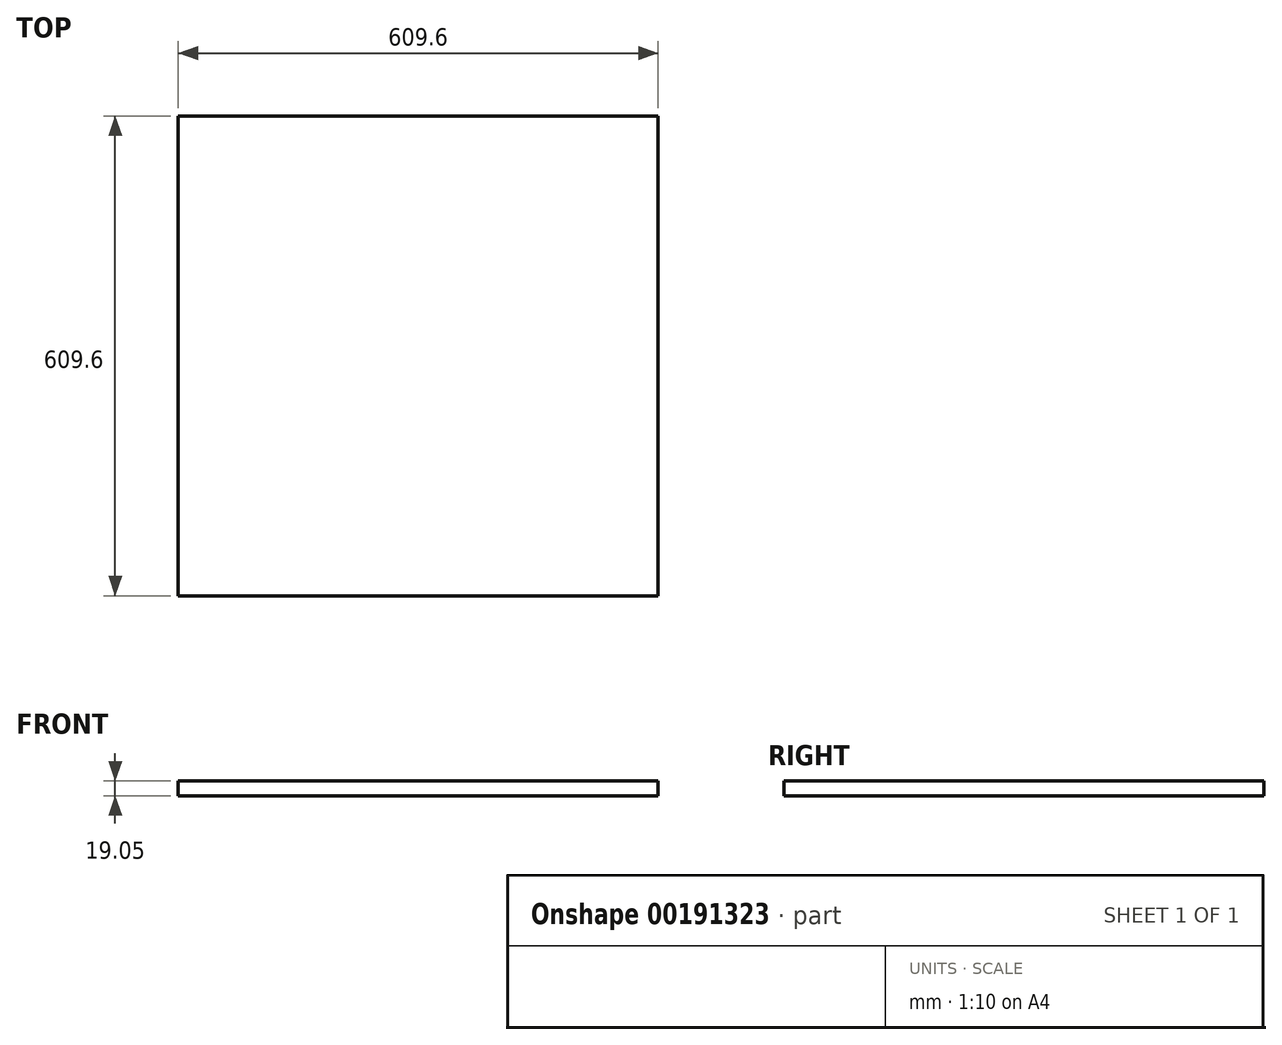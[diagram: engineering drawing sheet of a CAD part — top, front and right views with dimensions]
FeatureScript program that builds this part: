
annotation { "Feature Type Name" : "Feature", "Feature Type Description" : "" }
export const myFeature = defineFeature(function(context is Context, id is Id, definition is map)
    precondition{}
    {
        {
            var Q0;
            Q0=qCreatedBy(makeId("Top.planeOp"),FACE);
            var sketch = newSketch(context, id + "F0", { "sketchPlane" : qUnion([Q0])});
            skLineSegment(sketch, "E0.bottom", {"start": v(-304.8, 304.8) * mm, "end": v(304.8, 304.8) * mm});
            skLineSegment(sketch, "E0.top", {"start": v(-304.8, -304.8) * mm, "end": v(304.8, -304.8) * mm});
            skLineSegment(sketch, "E0.left", {"start": v(-304.8, 304.8) * mm, "end": v(-304.8, -304.8) * mm});
            skLineSegment(sketch, "E0.right", {"start": v(304.8, 304.8) * mm, "end": v(304.8, -304.8) * mm});
            skLineSegment(sketch, "E1", {"start": v(-304.8, 304.8) * mm, "end": v(304.8, -304.8) * mm, "construction": true});
            skSolve(sketch);
        }
        {
            var Q0;
            Q0=makeQuery(id+"F0.imprint","IMPRINT",FACE,{"disambiguationData":[TD([[makeQuery(id+"F0.imprint","IMPRINT",EDGE,{"derivedFrom":sQuery(id+"F0.wireOp",EDGE,"E0.bottom")}),-1.0]])]});
            extrude(context, id + "F1", {"entities" : qUnion([Q0]), "depth" : 19.05 * mm});
        }
    });
